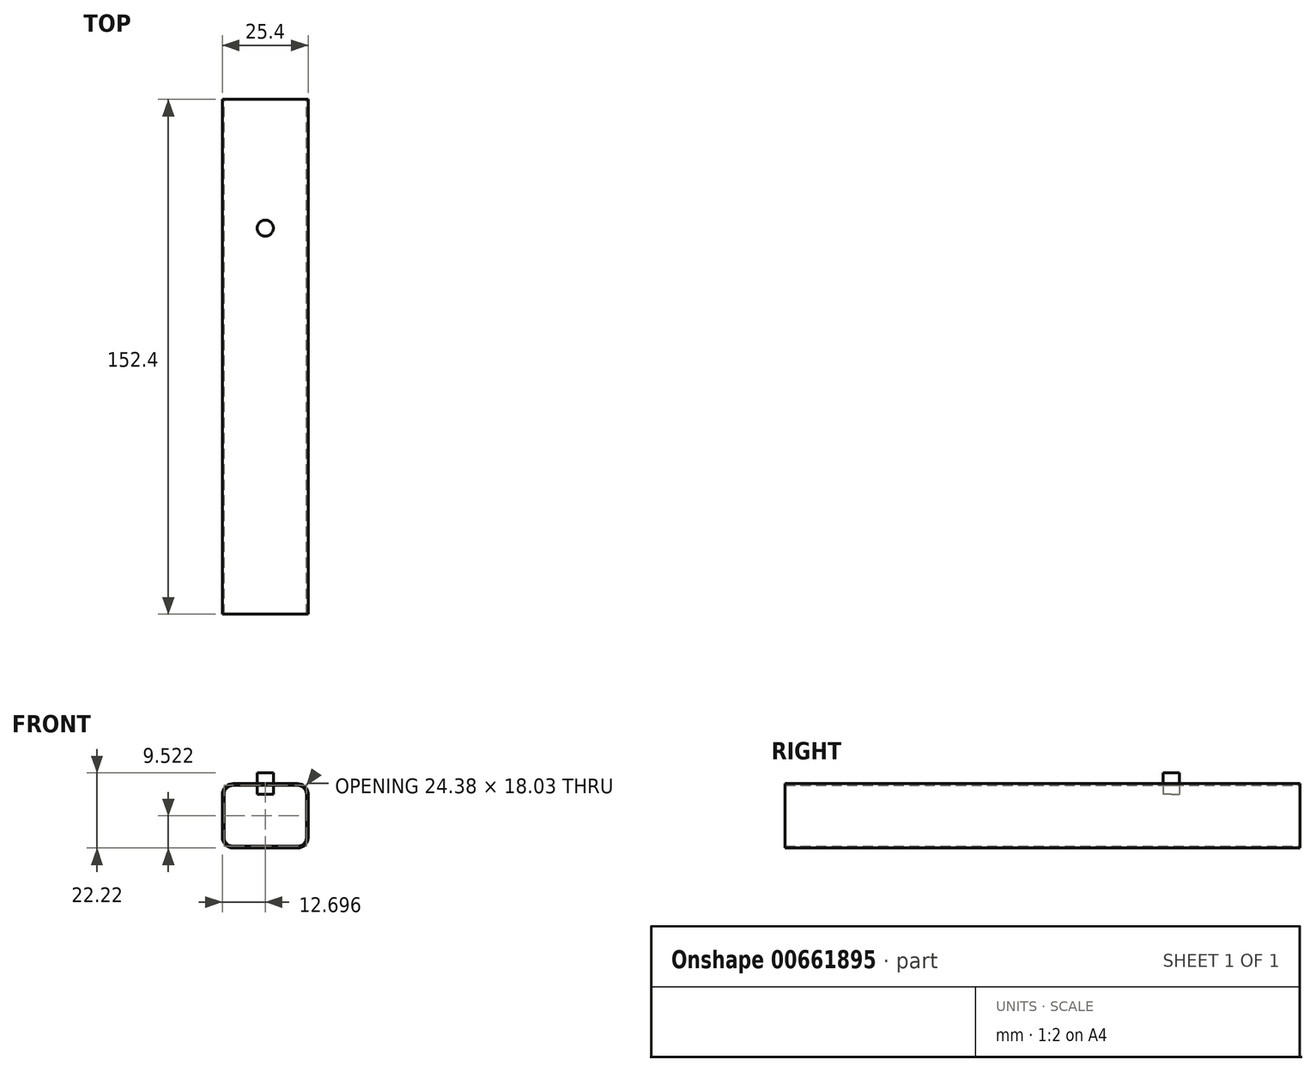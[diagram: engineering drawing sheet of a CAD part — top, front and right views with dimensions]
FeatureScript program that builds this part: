
annotation { "Feature Type Name" : "Feature", "Feature Type Description" : "" }
export const myFeature = defineFeature(function(context is Context, id is Id, definition is map)
    precondition{}
    {
        {
            var Q0;
            Q0=qCreatedBy(makeId("Front.planeOp"),FACE);
            var sketch = newSketch(context, id + "F0", { "sketchPlane" : qUnion([Q0])});
            skLineSegment(sketch, "E0.bottom", {"start": v(-38.84, -3.44) * mm, "end": v(-57.89, -3.44) * mm});
            skLineSegment(sketch, "E0.top", {"start": v(-38.84, 15.6) * mm, "end": v(-57.89, 15.6) * mm});
            skLineSegment(sketch, "E0.left", {"start": v(-35.66, -0.27) * mm, "end": v(-35.66, 12.43) * mm});
            skLineSegment(sketch, "E0.right", {"start": v(-61.06, -0.27) * mm, "end": v(-61.06, 12.43) * mm});
            skPoint(sketch, "E0.middle", {"position": v(-48.36, 6.08) * mm});
            skPoint(sketch, "E1.visualSharp", {"position": v(-61.06, 15.6) * mm});
            skArc(sketch, "E1.filletArc", {"start": v(-57.89, 15.6) * mm, "mid": v(-60.13, 14.68) * mm, "end": v(-61.06, 12.43) * mm});
            skPoint(sketch, "E2.visualSharp", {"position": v(-35.66, 15.6) * mm});
            skArc(sketch, "E2.filletArc", {"start": v(-35.66, 12.43) * mm, "mid": v(-36.6, 14.68) * mm, "end": v(-38.84, 15.6) * mm});
            skPoint(sketch, "E3.visualSharp", {"position": v(-35.66, -3.44) * mm});
            skArc(sketch, "E3.filletArc", {"start": v(-38.84, -3.44) * mm, "mid": v(-36.6, -2.51) * mm, "end": v(-35.66, -0.27) * mm});
            skPoint(sketch, "E4.visualSharp", {"position": v(-61.06, -3.44) * mm});
            skArc(sketch, "E4.filletArc", {"start": v(-61.06, -0.27) * mm, "mid": v(-60.13, -2.51) * mm, "end": v(-57.89, -3.44) * mm});
            skLineSegment(sketch, "E5.0", {"start": v(-60.56, -0.27) * mm, "end": v(-60.56, 12.43) * mm});
            skArc(sketch, "E5.1", {"start": v(-57.89, 15.1) * mm, "mid": v(-59.78, 14.32) * mm, "end": v(-60.56, 12.43) * mm});
            skArc(sketch, "E5.2", {"start": v(-60.56, -0.27) * mm, "mid": v(-59.78, -2.15) * mm, "end": v(-57.89, -2.94) * mm});
            skLineSegment(sketch, "E5.3", {"start": v(-38.84, 15.1) * mm, "end": v(-57.89, 15.1) * mm});
            skLineSegment(sketch, "E5.4", {"start": v(-38.84, -2.94) * mm, "end": v(-57.89, -2.94) * mm});
            skArc(sketch, "E5.5", {"start": v(-38.84, -2.94) * mm, "mid": v(-36.95, -2.15) * mm, "end": v(-36.17, -0.27) * mm});
            skLineSegment(sketch, "E5.6", {"start": v(-36.17, -0.27) * mm, "end": v(-36.17, 12.43) * mm});
            skArc(sketch, "E5.7", {"start": v(-36.17, 12.43) * mm, "mid": v(-36.95, 14.32) * mm, "end": v(-38.84, 15.1) * mm});
            skSolve(sketch);
        }
        {
            var Q0;
            Q0=makeQuery(id+"F0.imprint","IMPRINT",FACE,{"disambiguationData":[TD([[makeQuery(id+"F0.imprint","IMPRINT",EDGE,{"derivedFrom":sQuery(id+"F0.wireOp",EDGE,"E0.bottom")}),-1.0]])]});
            extrude(context, id + "F1", {"entities" : qUnion([Q0]), "depth" : 152.4 * mm, "offsetDistance" : 25.4 * mm});
        }
        {
            var Q0;
            Q0=makeQuery(id+"F1.opExtrude","SWEPT_FACE",FACE,{"disambiguationData":[OSD([sQuery(id+"F0.wireOp",EDGE,"E0.top")])]});
            cPlane(context, id + "F2", {"entities" : qUnion([Q0]), "cplaneType" : CPlaneType.OFFSET, "offset" : 0 * mm, "width" : 152.4 * mm, "height" : 152.4 * mm});
        }
        {
            var Q0;
            Q0=qCreatedBy(id+"F2.planeOp",FACE);
            var sketch = newSketch(context, id + "F3", { "sketchPlane" : qUnion([Q0])});
            skLineSegment(sketch, "E6", {"start": v(-48.36, 0) * mm, "end": v(-48.36, -508) * mm, "construction": true});
            skLineSegment(sketch, "E7", {"start": v(-62.62, -38.1) * mm, "end": v(-34.11, -38.1) * mm, "construction": true});
            skPoint(sketch, "E8", {"position": v(-48.36, -38.1) * mm});
            skCircle(sketch, "E9", {"center": v(-48.36, -38.1) * mm, "radius": 2.38 * mm});
            skSolve(sketch);
        }
        {
            var Q0;
            Q0=makeQuery(id+"F3.imprint","IMPRINT",FACE,{"disambiguationData":[TD([[makeQuery(id+"F3.imprint","IMPRINT",EDGE,{"derivedFrom":sQuery(id+"F3.wireOp",EDGE,"E9")}),1.0]])]});
            extrude(context, id + "F4", {"entities" : qUnion([Q0]), "operationType" : NewBodyOperationType.ADD, "endBound" : BoundingType.SYMMETRIC, "depth" : 6.35 * mm, "offsetDistance" : 25.4 * mm});
        }
    });
